FCSTD DOCUMENT  (FreeCAD 0.18R16131 (Git))
Label: Plate_200X570(3)
License: All rights reserved
LicenseURL: http://en.wikipedia.org/wiki/All_rights_reserved
objects: Sketcher::SketchObject×1, PartDesign::Body×1
note: 2 computed .brp shape members not serialized (recipe doc carries the construction recipe); baked Part::Feature solids carry a one-line shape summary decoded from their .brp

FEATURE [Sketcher::SketchObject] Sketch
  MapMode = 5
  Support = -> [XY_Plane]
  sketch-geometry (36):
    g0: LineSegment StartX=-384.886 StartY=-108.318 StartZ=0 EndX=185.114 EndY=-108.318 EndZ=0
    g1: LineSegment StartX=185.114 StartY=-108.318 StartZ=0 EndX=185.114 EndY=91.6818 EndZ=0
    g2: LineSegment StartX=185.114 StartY=91.6818 StartZ=0 EndX=-384.886 EndY=91.6818 EndZ=0
    g3: LineSegment StartX=-384.886 StartY=91.6818 StartZ=0 EndX=-384.886 EndY=-108.318 EndZ=0
    g4: ArcOfCircle CenterX=-360.539 CenterY=27.3515 CenterZ=0 NormalX=0 NormalY=0 NormalZ=1 AngleXU=0 Radius=2.5 StartAngle=1.5708 EndAngle=4.71239
    g5: ArcOfCircle CenterX=-260.539 CenterY=27.3515 CenterZ=0 NormalX=0 NormalY=0 NormalZ=1 AngleXU=0 Radius=2.5 StartAngle=4.71239 EndAngle=7.85398
    g6: LineSegment StartX=-360.539 StartY=24.8515 StartZ=0 EndX=-260.539 EndY=24.8515 EndZ=0
    g7: LineSegment StartX=-360.539 StartY=29.8515 StartZ=0 EndX=-260.539 EndY=29.8515 EndZ=0
    g8: ArcOfCircle CenterX=-359.944 CenterY=-44.1985 CenterZ=0 NormalX=0 NormalY=0 NormalZ=1 AngleXU=0 Radius=2.5 StartAngle=1.5708 EndAngle=4.71239
    g9: ArcOfCircle CenterX=-259.944 CenterY=-44.1985 CenterZ=0 NormalX=0 NormalY=0 NormalZ=1 AngleXU=0 Radius=2.5 StartAngle=4.71239 EndAngle=7.85398
    g10: LineSegment StartX=-359.944 StartY=-46.6985 StartZ=0 EndX=-259.944 EndY=-46.6985 EndZ=0
    g11: LineSegment StartX=-359.944 StartY=-41.6985 StartZ=0 EndX=-259.944 EndY=-41.6985 EndZ=0
    g12: ArcOfCircle CenterX=62.4822 CenterY=27.128 CenterZ=0 NormalX=0 NormalY=0 NormalZ=1 AngleXU=0 Radius=2.5 StartAngle=1.5708 EndAngle=4.71239
    g13: ArcOfCircle CenterX=162.482 CenterY=27.128 CenterZ=0 NormalX=0 NormalY=0 NormalZ=1 AngleXU=0 Radius=2.5 StartAngle=4.71239 EndAngle=7.85398
    g14: LineSegment StartX=62.4822 StartY=24.628 StartZ=0 EndX=162.482 EndY=24.628 EndZ=0
    g15: LineSegment StartX=62.4822 StartY=29.628 StartZ=0 EndX=162.482 EndY=29.628 EndZ=0
    g16: ArcOfCircle CenterX=63.0777 CenterY=-43.8759 CenterZ=0 NormalX=0 NormalY=0 NormalZ=1 AngleXU=0 Radius=2.5 StartAngle=1.5708 EndAngle=4.71239
    g17: ArcOfCircle CenterX=163.078 CenterY=-43.8759 CenterZ=0 NormalX=0 NormalY=0 NormalZ=1 AngleXU=0 Radius=2.5 StartAngle=4.71239 EndAngle=7.85398
    g18: LineSegment StartX=63.0777 StartY=-46.3759 StartZ=0 EndX=163.078 EndY=-46.3759 EndZ=0
    g19: LineSegment StartX=63.0777 StartY=-41.3759 StartZ=0 EndX=163.078 EndY=-41.3759 EndZ=0
    g20: ArcOfCircle CenterX=-360.844 CenterY=11.6818 CenterZ=0 NormalX=0 NormalY=0 NormalZ=1 AngleXU=0 Radius=2 StartAngle=1.5708 EndAngle=4.71239
    g21: ArcOfCircle CenterX=-318.844 CenterY=11.6818 CenterZ=0 NormalX=0 NormalY=0 NormalZ=1 AngleXU=0 Radius=2 StartAngle=4.71239 EndAngle=7.85398
    g22: LineSegment StartX=-360.844 StartY=9.6818 StartZ=0 EndX=-318.844 EndY=9.6818 EndZ=0
    g23: LineSegment StartX=-360.844 StartY=13.6818 StartZ=0 EndX=-318.844 EndY=13.6818 EndZ=0
    g24: ArcOfCircle CenterX=-360.544 CenterY=-28.3182 CenterZ=0 NormalX=0 NormalY=0 NormalZ=1 AngleXU=0 Radius=2 StartAngle=1.5708 EndAngle=4.71239
    g25: ArcOfCircle CenterX=-318.544 CenterY=-28.3182 CenterZ=0 NormalX=0 NormalY=0 NormalZ=1 AngleXU=0 Radius=2 StartAngle=4.71239 EndAngle=7.85398
    g26: LineSegment StartX=-360.544 StartY=-30.3182 StartZ=0 EndX=-318.544 EndY=-30.3182 EndZ=0
    g27: LineSegment StartX=-360.544 StartY=-26.3182 StartZ=0 EndX=-318.544 EndY=-26.3182 EndZ=0
    g28: ArcOfCircle CenterX=120.208 CenterY=13.2757 CenterZ=0 NormalX=0 NormalY=0 NormalZ=1 AngleXU=0 Radius=2 StartAngle=1.5708 EndAngle=4.71239
    g29: ArcOfCircle CenterX=162.208 CenterY=13.2757 CenterZ=0 NormalX=0 NormalY=0 NormalZ=1 AngleXU=0 Radius=2 StartAngle=4.71239 EndAngle=7.85398
    g30: LineSegment StartX=120.208 StartY=11.2757 StartZ=0 EndX=162.208 EndY=11.2757 EndZ=0
    g31: LineSegment StartX=120.208 StartY=15.2757 StartZ=0 EndX=162.208 EndY=15.2757 EndZ=0
    g32: ArcOfCircle CenterX=120.507 CenterY=-26.7243 CenterZ=0 NormalX=0 NormalY=0 NormalZ=1 AngleXU=0 Radius=2 StartAngle=1.5708 EndAngle=4.71239
    g33: ArcOfCircle CenterX=162.507 CenterY=-26.7243 CenterZ=0 NormalX=0 NormalY=0 NormalZ=1 AngleXU=0 Radius=2 StartAngle=4.71239 EndAngle=7.85398
    g34: LineSegment StartX=120.507 StartY=-28.7243 StartZ=0 EndX=162.507 EndY=-28.7243 EndZ=0
    g35: LineSegment StartX=120.507 StartY=-24.7243 StartZ=0 EndX=162.507 EndY=-24.7243 EndZ=0
  constraints (78):
    c: Coincident(g0,g1)
    c: Coincident(g1,g2)
    c: Coincident(g2,g3)
    c: Coincident(g3,g0)
    c: Horizontal(g0)
    c: Horizontal(g2)
    c: Vertical(g1)
    c: Vertical(g3)
    c: DistanceX(g2,g2) = 570
    c: DistanceY(g3,g3) = 200
    c: Tangent(g4,g7) = 1.5708
    c: Tangent(g4,g6) = -1.5708
    c: Tangent(g6,g5) = -1.5708
    c: Tangent(g7,g5) = 1.5708
    c: Horizontal(g6)
    c: Equal(g4,g5)
    c: DistanceX(g7,g7) = 100
    c: DistanceY(g4,g4) = 5
    c: Tangent(g8,g11) = 1.5708
    c: Tangent(g8,g10) = -1.5708
    c: Tangent(g10,g9) = -1.5708
    c: Tangent(g11,g9) = 1.5708
    c: Horizontal(g10)
    c: Equal(g8,g9)
    c: DistanceX(g11,g11) = 100
    c: DistanceY(g8,g8) = 5
    c: Tangent(g12,g15) = 1.5708
    c: Tangent(g12,g14) = -1.5708
    c: Tangent(g14,g13) = -1.5708
    c: Tangent(g15,g13) = 1.5708
    c: Horizontal(g14)
    c: Equal(g12,g13)
    c: Equal(g7,g15) = 100
    c: Equal(g4,g12) = 5
    c: Tangent(g16,g19) = 1.5708
    c: Tangent(g16,g18) = -1.5708
    c: Tangent(g18,g17) = -1.5708
    c: Tangent(g19,g17) = 1.5708
    c: Horizontal(g18)
    c: Equal(g16,g17)
    c: Equal(g11,g19) = 100
    c: Equal(g8,g16) = 5
    c: Tangent(g20,g23) = 1.5708
    c: Tangent(g20,g22) = -1.5708
    c: Tangent(g22,g21) = -1.5708
    c: Tangent(g23,g21) = 1.5708
    c: Horizontal(g22)
    c: Equal(g20,g21)
    c: DistanceX(g23,g23) = 42
    c: DistanceY(g20,g20) = 4
    c: Tangent(g24,g27) = 1.5708
    c: Tangent(g24,g26) = -1.5708
    c: Tangent(g26,g25) = -1.5708
    c: Tangent(g27,g25) = 1.5708
    c: Horizontal(g26)
    c: Equal(g24,g25)
    c: Equal(g23,g27) = 42
    c: Equal(g20,g24) = 4
    c: DistanceY(g24,g20) = 40
    c: DistanceY(g20,g2) = 80
    c: Tangent(g28,g31) = 1.5708
    c: Tangent(g28,g30) = -1.5708
    c: Tangent(g30,g29) = -1.5708
    c: Tangent(g31,g29) = 1.5708
    c: Horizontal(g30)
    c: Equal(g28,g29)
    c: Equal(g23,g31) = 42
    c: Equal(g20,g28) = 4
    c: Tangent(g32,g35) = 1.5708
    c: Tangent(g32,g34) = -1.5708
    c: Tangent(g34,g33) = -1.5708
    c: Tangent(g35,g33) = 1.5708
    c: Horizontal(g34)
    c: Equal(g32,g33)
    c: Equal(g31,g35) = 42
    c: Equal(g28,g32) = 4
    c: DistanceY(g32,g28) = 40
    c: DistanceY(g8,g4) = 71.55
FEATURE [PartDesign::Body] Body
  Group = -> [Sketch]
  Origin = -> Origin
